# Revit family: Faucet-Deck_Mount-Bath-KOHLER-MEMOIRS-K-469T
name_source: partatom
category: Plumbing Fixtures
revit_build: Autodesk Revit 2017 (Build: 20160225_1515(x64)
units: mm (PartAtom-declared; Revit-internal decimal feet)

## family parameters
Cut with Voids When Loaded = No
Host = Face
OmniClass Number = 23.31.11.00
OmniClass Title = Faucets
Part Type = Normal
Room Calculation Point = No
Round Connector Dimension = Use Diameter
Shared = No

## types (10) — shared parameters
ADA Compliant = No
Assembly Code = D2010
CW Connection = Yes
Cold Water Inlet = Cold Water Inlet
Date Modified = 08/29/2020
Default Elevation = 36"
Description = STATELY DECK/RIM MT FAUCET
Drain Included = No
Flow Rate = 0 GPM
HW Connection = Yes
Height = 4 15/16"
Hot Water Inlet = Hot Water Inlet
Length = 6 5/16"
Manufacturer = KOHLER Co.
Master Format 2014 = 22.41.39
Master Format 2014 Name = Residential Faucets, Supplies, and Trim
Material = Premium Metal Construction
Pressure = 0.00 psi
Product Documentation Link = https://files.kohler.com.cn
Product Name = Memoirs
Product Page URL = https://www.kohler.com.cn
Spout Reach = 6 5/16"
URL = http://www.kohler.com.cn
Vent Connection = No
Waste Connection = No
Waste Water Outlet = Waste Water Outlet
WaterSense Certified = No

## per-type parameters (varying)
| type | Cross Handle | Deco Lever Handle | Dist1 | Finish | Handle Clearance | Model | Type |
| Deco Lever Handle, CP-Polished Chrome | No | Yes | 0" | Kohler-Metal-CP-Polished_Chrome | 2 3/4" | K-469T-4V-CP | 1 |
| Deco Lever Handle, AF-Vibrant French Gold | No | Yes | 0" | Kohler-Metal-AF-Vibrant_French_Gold | 2 3/4" | K-469T-4V-AF | 2 |
| Deco Lever Handle, RGD-Rose Gold | No | Yes | 0" | Kohler-Metal-RGD-Rose_Gold | 2 3/4" | K-469T-4V-RGD | 3 |
| Deco Lever Handle, BN-Vibrant Brushed Nickel | No | Yes | 0" | Kohler-Metal-BN-Vibrant_Brushed_Nickel | 2 3/4" | K-469T-4V-BN | 4 |
| Deco Lever Handle, SN-Champagne Gold | No | Yes | 0" | Kohler-Metal-SN-Champagne_Gold | 2 3/4" | K-469T-4V-SN | 5 |
| Crossr Handle, CP-Polished Chrome | Yes | No | 1 1/2" | Kohler-Metal-CP-Polished_Chrome | 1 1/2" | K-469T-3S-CP | 6 |
| Crossr Handle, AF-Vibrant French Gold | Yes | No | 1 1/2" | Kohler-Metal-AF-Vibrant_French_Gold | 1 1/2" | K-469T-3S-AF | 7 |
| Cross Handle, RGD-Rose Gold | Yes | No | 1 1/2" | Kohler-Metal-RGD-Rose_Gold | 1 1/2" | K-469T-3S-RGD | 8 |
| Cross Handle, BN-Vibrant Brushed Nickel | Yes | No | 1 1/2" | Kohler-Metal-BN-Vibrant_Brushed_Nickel | 1 1/2" | K-469T-3S-BN | 9 |
| Cross  Handle, SN-Champagne Gold | Yes | No | 1 1/2" | Kohler-Metal-SN-Champagne_Gold | 1 1/2" | K-469T-3S-SN | 10 |

## geometry (parser evidence)
native form markers: Sweep x6
no freeform markers — native parametric forms only
